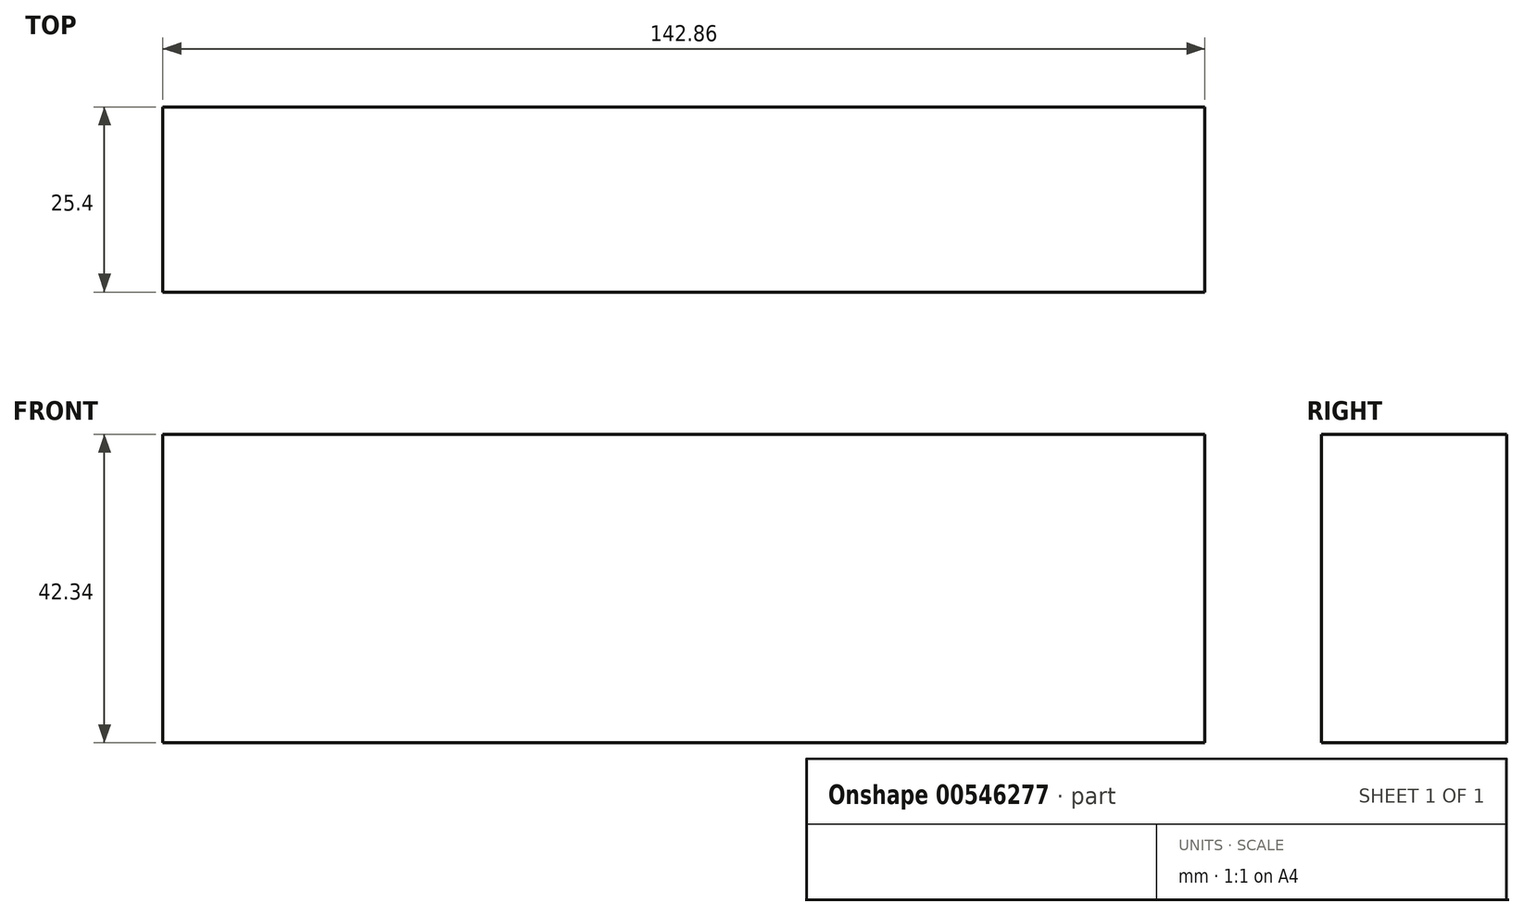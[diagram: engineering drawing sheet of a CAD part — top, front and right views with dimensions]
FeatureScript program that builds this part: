
annotation { "Feature Type Name" : "Feature", "Feature Type Description" : "" }
export const myFeature = defineFeature(function(context is Context, id is Id, definition is map)
    precondition{}
    {
        {
            var Q0;
            Q0=qCreatedBy(makeId("Front.planeOp"),FACE);
            var sketch = newSketch(context, id + "F0", { "sketchPlane" : qUnion([Q0])});
            skLineSegment(sketch, "E0.bottom", {"start": v(-71.43, 21.17) * mm, "end": v(71.43, 21.17) * mm});
            skLineSegment(sketch, "E0.top", {"start": v(-71.43, -21.17) * mm, "end": v(71.43, -21.17) * mm});
            skLineSegment(sketch, "E0.left", {"start": v(-71.43, 21.17) * mm, "end": v(-71.43, -21.17) * mm});
            skLineSegment(sketch, "E0.right", {"start": v(71.43, 21.17) * mm, "end": v(71.43, -21.17) * mm});
            skPoint(sketch, "E0.middle", {"position": v(0, 0) * mm});
            skLineSegment(sketch, "E1.bottom", {"start": v(-191.13, 37.55) * mm, "end": v(-101.92, 37.55) * mm});
            skLineSegment(sketch, "E1.top", {"start": v(-191.13, -14.4) * mm, "end": v(-101.92, -14.4) * mm});
            skLineSegment(sketch, "E1.left", {"start": v(-191.13, 37.55) * mm, "end": v(-191.13, -14.4) * mm});
            skLineSegment(sketch, "E1.right", {"start": v(-101.92, 37.55) * mm, "end": v(-101.92, -14.4) * mm});
            skPoint(sketch, "E1.middle", {"position": v(-146.52, 11.57) * mm});
            skLineSegment(sketch, "E2", {"start": v(-71.43, 21.17) * mm, "end": v(-71.43, 76.5) * mm});
            skLineSegment(sketch, "E3", {"start": v(-71.43, 76.5) * mm, "end": v(-82.16, 83.85) * mm});
            skPoint(sketch, "E4.endSnap0", {"position": v(-65.78, 96.83) * mm});
            skArc(sketch, "E5", {"start": v(-82.16, 83.85) * mm, "mid": v(-97.1, 80.36) * mm, "end": v(-92.32, 65.78) * mm});
            skLineSegment(sketch, "E6", {"start": v(-92.32, 65.78) * mm, "end": v(-71.43, -21.17) * mm});
            skLineSegment(sketch, "E7.0", {"start": v(-108.6, 55.25) * mm, "end": v(-89.2, -25.44) * mm});
            skArc(sketch, "E7.1", {"start": v(-71.83, 98.94) * mm, "mid": v(-109.98, 93.73) * mm, "end": v(-108.6, 55.25) * mm});
            skLineSegment(sketch, "E7.2", {"start": v(-61.1, 91.6) * mm, "end": v(-71.83, 98.94) * mm});
            skSolve(sketch);
        }
        {
            var Q0;
            Q0=makeQuery(id+"F0.imprint","IMPRINT",FACE,{"disambiguationData":[TD([[makeQuery(id+"F0.imprint","IMPRINT",EDGE,{"derivedFrom":sQuery(id+"F0.wireOp",EDGE,"E0.bottom")}),-1.0]])]});
            extrude(context, id + "F1", {"entities" : qUnion([Q0]), "depth" : 25.4 * mm, "offsetDistance" : 25.4 * mm});
        }
    });
